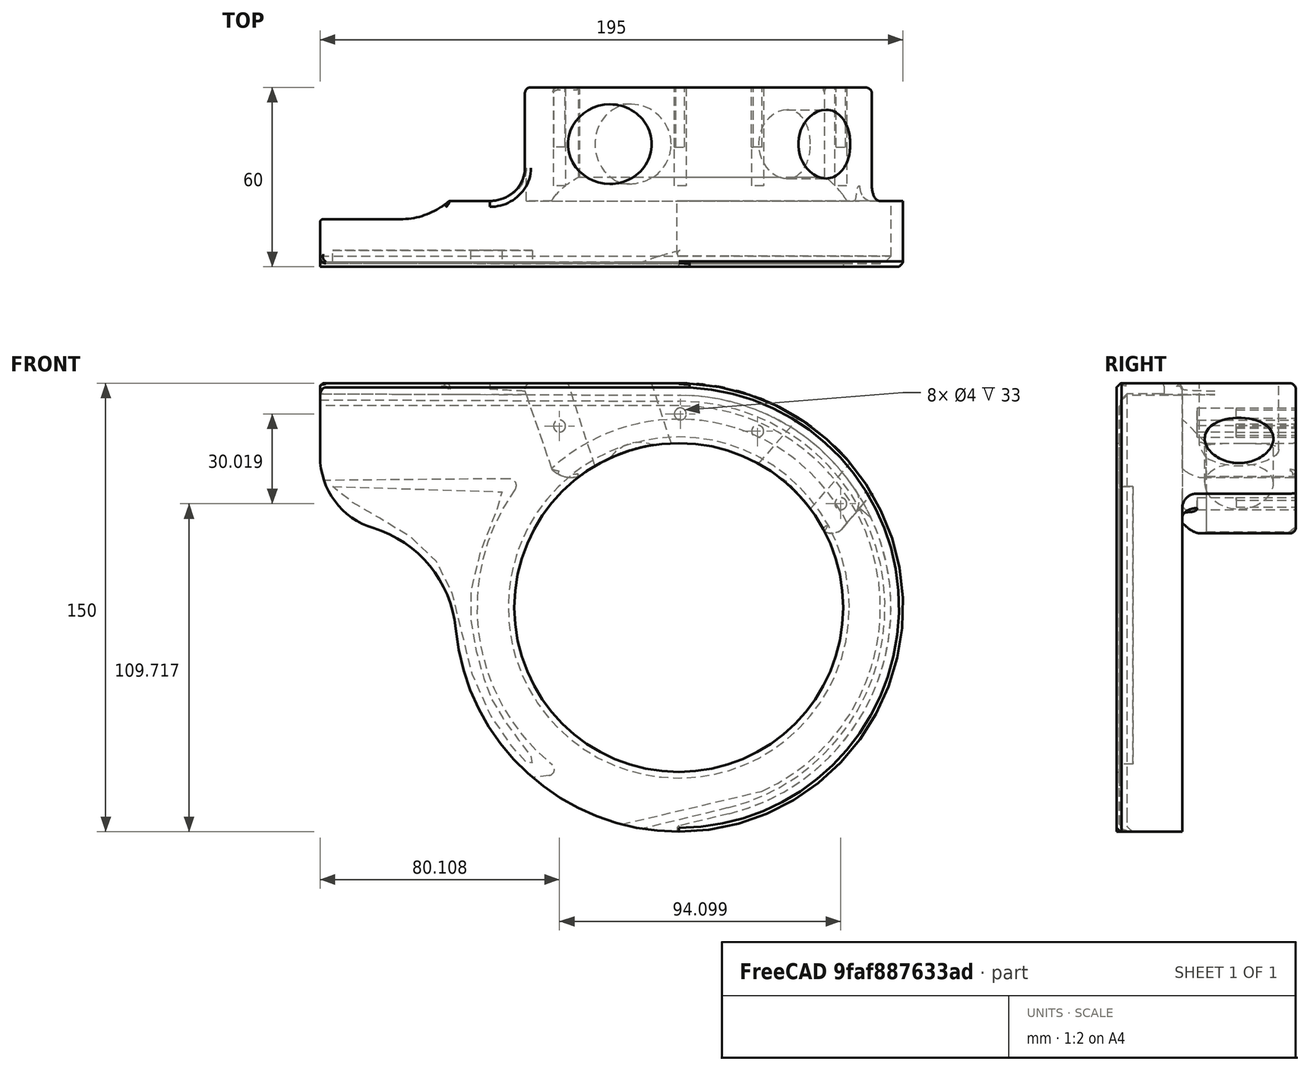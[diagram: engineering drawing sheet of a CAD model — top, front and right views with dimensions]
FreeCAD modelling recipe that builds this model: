
FCSTD DOCUMENT  (FreeCAD 0.19R)
Label: BottomWhiteBike6
License: All rights reserved
LicenseURL: http://en.wikipedia.org/wiki/All_rights_reserved
objects: Sketcher::SketchObject×10, PartDesign::Fillet×9, PartDesign::Pocket×7, PartDesign::Pad×2, Part::Cylinder×2, PartDesign::Chamfer×2, Part::MultiFuse×1, PartDesign::Groove×1, PartDesign::Body×1, Part::Cut×1, Mesh::Feature×1
note: 57 computed .brp shape members not serialized (recipe doc carries the construction recipe); baked Part::Feature solids carry a one-line shape summary decoded from their .brp

FEATURE [Sketcher::SketchObject] Sketch
  FullyConstrained = false
  MapMode = 5
  Placement = pos=(0,0,0) rot=(1,0,0;1.5708rad)
  Support = -> [XZ_Plane]
  sketch-geometry (11):
    g0: LineSegment StartX=0 StartY=0 StartZ=0 EndX=112.706 EndY=65.0706 EndZ=0
    g1: LineSegment StartX=0 StartY=0 StartZ=0 EndX=7.3e-15 EndY=119.149 EndZ=0
    g2: LineSegment StartX=2.14e-14 StartY=70 StartZ=0 EndX=-199.884 EndY=70 EndZ=0
    g3: Circle CenterX=0 CenterY=0 CenterZ=0 NormalX=0 NormalY=0 NormalZ=1 AngleXU=0 Radius=45
    g4: ArcOfCircle CenterX=0 CenterY=0 CenterZ=0 NormalX=0 NormalY=0 NormalZ=1 AngleXU=0 Radius=70 StartAngle=3.5224 EndAngle=7.85398
    g5: LineSegment StartX=-120 StartY=75 StartZ=0 EndX=2.84e-14 EndY=75 EndZ=0
    g6: ArcOfCircle CenterX=0 CenterY=0 CenterZ=0 NormalX=0 NormalY=0 NormalZ=1 AngleXU=0 Radius=75 StartAngle=3.23571 EndAngle=7.85398
    g7: LineSegment StartX=-120 StartY=75 StartZ=0 EndX=-120 EndY=50.5061 EndZ=0
    g8: ArcOfCircle CenterX=-95 CenterY=50.5061 CenterZ=0 NormalX=0 NormalY=0 NormalZ=1 AngleXU=0 Radius=25 StartAngle=3.14159 EndAngle=4.4201
    g9: Circle CenterX=0 CenterY=0 CenterZ=0 NormalX=0 NormalY=0 NormalZ=1 AngleXU=0 Radius=55
    g10: ArcOfCircle CenterX=-113.419 CenterY=-10.7061 CenterZ=0 NormalX=0 NormalY=0 NormalZ=1 AngleXU=0 Radius=38.9235 StartAngle=0.0941155 EndAngle=1.27851
  constraints (25):
    c: Coincident(g0,g-1)
    c: Coincident(g1,g-1)
    c: Angle(g1) = 1.5708
    c: Angle(g0,g1) = 1.0472
    c: PointOnObject(g2,g1)
    c: Angle(g2) = 3.14159
    c: DistanceY(g2) = 70
    c: Coincident(g3,g-1)
    c: Coincident(g4,g-1)
    c: Diameter(g3) = 90
    c: Coincident(g4,g2)
    c: PointOnObject(g5,g1)
    c: Horizontal(g5)
    c: Coincident(g6,g-1)
    c: Coincident(g6,g5)
    c: Coincident(g5,g7)
    c: Vertical(g7)
    c: Tangent(g8,g7) = -1.5708
    c: Diameter(g6) = 150
    c: Distance(g5) = 120
    c: Diameter(g8) = 50
    c: Coincident(g9,g6)
    c: Diameter(g9) = 110
    c: Tangent(g10,g6) = 1.5708
    c: Tangent(g10,g8) = 1.5708
FEATURE [PartDesign::Pad] Pad
  Direction = (1,1,1)
  Length = 40
  Length2 = 20
  Placement = pos=(0,0,0) rot=(1,0,0;1.5708rad)
  Profile = -> Sketch
  Type = 4
FEATURE [Sketcher::SketchObject] Sketch001
  FullyConstrained = false
  MapMode = 5
  Placement = pos=(0,20,-4.4e-15) rot=(-1,0,0;1.5708rad)
  Support = -> [Pad]
  sketch-geometry (14):
    g0: GeomPoint X=0 Y=0 Z=0
    g1: LineSegment StartX=0 StartY=0 StartZ=0 EndX=101.779 EndY=-121.295 EndZ=0
    g2: LineSegment StartX=54.9288 StartY=-26.5684 StartZ=0 EndX=75.9423 EndY=-51.6114 EndZ=0
    g3: ArcOfCircle CenterX=0 CenterY=0 CenterZ=0 NormalX=0 NormalY=0 NormalZ=1 AngleXU=0 Radius=91.8204 StartAngle=5.68627 EndAngle=9.42478
    g4: LineSegment StartX=-211.759 StartY=-107.924 StartZ=0 EndX=-91.8204 EndY=2.84e-14 EndZ=0
    g5: LineSegment StartX=43.6212 StartY=-30.5051 StartZ=0 EndX=-31.6726 EndY=-44.3314 EndZ=0
    g6: LineSegment StartX=-42.2439 StartY=-45.8964 StartZ=0 EndX=-52.4011 EndY=-75.3951 EndZ=0
    g7: LineSegment StartX=0 StartY=0 StartZ=0 EndX=-69.9978 EndY=-203.289 EndZ=0
    g8: ArcOfCircle CenterX=51.1344 CenterY=-29.7522 CenterZ=0 NormalX=0 NormalY=0 NormalZ=1 AngleXU=0 Radius=4.95311 StartAngle=0.698132 EndAngle=2.38613
    g9: LineSegment StartX=47.5288 StartY=-26.3563 StartZ=0 EndX=43.6212 EndY=-30.5051 EndZ=0
    g10: LineSegment StartX=-52.4011 StartY=-75.3951 StartZ=0 EndX=-16.4761 EndY=-75.3951 EndZ=0
    g11: LineSegment StartX=-16.4761 StartY=-75.3951 StartZ=0 EndX=-30.9733 EndY=-107.924 EndZ=0
    g12: LineSegment StartX=-30.9733 StartY=-107.924 StartZ=0 EndX=-211.759 EndY=-107.924 EndZ=0
    g13: ArcOfCircle CenterX=-35.7204 CenterY=-53.4756 CenterZ=0 NormalX=0 NormalY=0 NormalZ=1 AngleXU=0 Radius=10 StartAngle=1.15406 EndAngle=2.28148
  constraints (24):
    c: Coincident(g1,g-1)
    c: Angle(g1,g-2) = 2.44346
    c: Coincident(g3,g-1)
    c: PointOnObject(g3,g-1)
    c: Coincident(g4,g3)
    c: Distance(g2,g1) = 25
    c: Parallel(g2,g1)
    c: Coincident(g7,g3)
    c: Angle(g7,g1) = 1.02974
    c: Parallel(g7,g6)
    c: Distance(g6,g7) = 25
    c: Tangent(g8,g2) = 1.5708
    c: Tangent(g9,g8) = -1.5708
    c: Coincident(g5,g9)
    c: Horizontal(g10)
    c: Coincident(g11,g10)
    c: Coincident(g12,g11)
    c: Coincident(g12,g4)
    c: Horizontal(g12)
    c: Coincident(g6,g13)
    c: Radius(g13) = 10
    c: Coincident(g13,g5)
    c: Coincident(g2,g3)
    c: Coincident(g10,g6)
FEATURE [PartDesign::Pocket] Pocket  label="FirstPocket-trim"
  BaseFeature = -> Pad
  Length = 38
  Length2 = 100
  Placement = pos=(0,0,0) rot=(1,0,0;1.5708rad)
  Profile = -> Sketch001
  Type = 0
FEATURE [Sketcher::SketchObject] Sketch003
  FullyConstrained = false
  MapMode = 5
  Placement = pos=(0,-18,7.9e-15) rot=(-1,0,0;1.5708rad)
  Support = -> [Pocket]
  sketch-geometry (5):
    g0: ArcOfCircle CenterX=0 CenterY=0 CenterZ=0 NormalX=0 NormalY=0 NormalZ=1 AngleXU=0 Radius=71 StartAngle=4.71239 EndAngle=7.61456
    g1: LineSegment StartX=-204.417 StartY=-71.8091 StartZ=0 EndX=0 EndY=-71 EndZ=0
    g2: LineSegment StartX=16.837 StartY=68.9748 StartZ=0 EndX=-53.1835 EndY=86.067 EndZ=0
    g3: LineSegment StartX=-53.1835 StartY=86.067 StartZ=0 EndX=-158.302 EndY=56.4495 EndZ=0
    g4: LineSegment StartX=-158.302 StartY=56.4495 StartZ=0 EndX=-204.417 EndY=-71.8091 EndZ=0
  constraints (8):
    c: Coincident(g0,g-1)
    c: PointOnObject(g0,g-2)
    c: Diameter(g0) = 142
    c: Coincident(g1,g0)
    c: Tangent(g0,g2) = -1.5708
    c: Coincident(g2,g3)
    c: Coincident(g3,g4)
    c: Coincident(g4,g1)
FEATURE [PartDesign::Pocket] Pocket001  label="2ndPocket-thk"
  BaseFeature = -> Pocket
  Length = 20.5
  Length2 = 0
  Placement = pos=(0,0,0) rot=(1,0,0;1.5708rad)
  Profile = -> Sketch003
  Type = 4
FEATURE [Part::Cylinder] Cylinder  label="DT"
  Angle = 360
  AttacherType = Attacher::AttachEngine3D
  Height = 156
  Placement = pos=(1,1,1) rot=(0,1,0;0.715585rad)
  Radius = 11.5
FEATURE [Part::Cylinder] Cylinder001  label="ST"
  Angle = 360
  AttacherType = Attacher::AttachEngine3D
  Height = 150
  Placement = pos=(1,1,1) rot=(0,-1,0;0.314159rad)
  Radius = 13.3
FEATURE [Part::MultiFuse] Fusion
  Shapes = -> [Cylinder,Cylinder001]
FEATURE [Sketcher::SketchObject] Sketch004
  FullyConstrained = false
  MapMode = 5
  Placement = pos=(0,-38,4.2e-14) rot=(0,0.707107,0.707107;3.14159rad)
  sketch-geometry (11):
    g0: ArcOfCircle CenterX=0 CenterY=0 CenterZ=0 NormalX=0 NormalY=0 NormalZ=1 AngleXU=0 Radius=67.4561 StartAngle=1.5708 EndAngle=4.28769
    g1: LineSegment StartX=43.378 StartY=-56.1672 StartZ=0 EndX=97.643 EndY=-63.0707 EndZ=0
    g2: LineSegment StartX=97.643 StartY=-63.0707 StartZ=0 EndX=64.3329 EndY=-83.232 EndZ=0
    g3: LineSegment StartX=64.3329 StartY=-83.232 StartZ=0 EndX=-27.7948 EndY=-61.4636 EndZ=0
    g4: Circle CenterX=0 CenterY=0 CenterZ=0 NormalX=0 NormalY=0 NormalZ=1 AngleXU=0 Radius=57.041
    g5: LineSegment StartX=4.1e-15 StartY=67.4561 StartZ=0 EndX=181.167 EndY=67.4561 EndZ=0
    g6: ArcOfCircle CenterX=0 CenterY=0 CenterZ=0 NormalX=0 NormalY=0 NormalZ=1 AngleXU=0 Radius=67.5078 StartAngle=5.39067 EndAngle=6.9075
    g7: LineSegment StartX=56.6391 StartY=43.0635 StartZ=0 EndX=192.151 EndY=41.8244 EndZ=0
    g8: LineSegment StartX=192.151 StartY=41.8244 StartZ=0 EndX=181.167 EndY=67.4561 EndZ=0
    g9: ArcOfCircle CenterX=56.6183 CenterY=40.7899 CenterZ=0 NormalX=0 NormalY=0 NormalZ=1 AngleXU=0 Radius=2.27364 StartAngle=1.56165 EndAngle=3.7659
    g10: ArcOfCircle CenterX=43.6348 CenterY=-54.1491 CenterZ=0 NormalX=0 NormalY=0 NormalZ=1 AngleXU=0 Radius=2.03437 StartAngle=2.24908 EndAngle=4.58585
  constraints (15):
    c: Coincident(g0,g-1)
    c: Coincident(g2,g1)
    c: Coincident(g3,g2)
    c: Coincident(g3,g0)
    c: Coincident(g4,g0)
    c: PointOnObject(g0,g-2)
    c: Coincident(g5,g0)
    c: Horizontal(g5)
    c: Coincident(g6,g0)
    c: Coincident(g7,g8)
    c: Coincident(g8,g5)
    c: Tangent(g6,g9) = 1.5708
    c: Tangent(g7,g9) = 1.5708
    c: Tangent(g1,g10) = -1.5708
    c: Tangent(g6,g10) = 1.5708
FEATURE [PartDesign::Pocket] Pocket002  label="ChainGroove"
  BaseFeature = -> Pocket001
  Length = 1
  Length2 = 100
  Placement = pos=(0,0,0) rot=(1,0,0;1.5708rad)
  Profile = -> Sketch004
  Type = 0
FEATURE [Sketcher::SketchObject] Sketch006
  FullyConstrained = false
  MapMode = 5
  Placement = pos=(0,20,-1.8e-14) rot=(-1,0,0;1.5708rad)
  sketch-geometry (4):
    g0: Circle CenterX=-39.8919 CenterY=-60.6956 CenterZ=0 NormalX=0 NormalY=0 NormalZ=1 AngleXU=0 Radius=2
    g1: Circle CenterX=0.518637 CenterY=-64.7366 CenterZ=0 NormalX=0 NormalY=0 NormalZ=1 AngleXU=0 Radius=2
    g2: Circle CenterX=26.4007 CenterY=-58.9637 CenterZ=0 NormalX=0 NormalY=0 NormalZ=1 AngleXU=0 Radius=2
    g3: Circle CenterX=54.207 CenterY=-34.7174 CenterZ=0 NormalX=0 NormalY=0 NormalZ=1 AngleXU=0 Radius=2
  constraints (4):
    c: Diameter(g0) = 4
    c: Equal(g0,g1)
    c: Equal(g0,g2)
    c: Equal(g0,g3)
FEATURE [Sketcher::SketchObject] Sketch007
  FullyConstrained = false
  MapMode = 5
  Placement = pos=(0,20,-1.99e-14) rot=(-1,0,0;1.5708rad)
  sketch-geometry (4):
    g0: Circle CenterX=-39.9046 CenterY=-60.6617 CenterZ=0 NormalX=0 NormalY=0 NormalZ=1 AngleXU=0 Radius=2
    g1: Circle CenterX=0.50043 CenterY=-64.7556 CenterZ=0 NormalX=0 NormalY=0 NormalZ=1 AngleXU=0 Radius=2
    g2: Circle CenterX=26.3703 CenterY=-58.9325 CenterZ=0 NormalX=0 NormalY=0 NormalZ=1 AngleXU=0 Radius=2
    g3: Circle CenterX=54.2248 CenterY=-34.7424 CenterZ=0 NormalX=0 NormalY=0 NormalZ=1 AngleXU=0 Radius=2
  constraints (4):
    c: Diameter(g0) = 4
    c: Equal(g0,g1)
    c: Equal(g0,g2)
    c: Equal(g0,g3)
FEATURE [PartDesign::Chamfer] Chamfer
  Angle = 45
  Base = -> Pocket002 [Edge39]
  BaseFeature = -> Pocket002
  ChamferType = 0
  FlipDirection = false
  Placement = pos=(0,0,0) rot=(1,0,0;1.5708rad)
  Size = 2
  Size2 = 1
  SupportTransform = false
FEATURE [PartDesign::Fillet] Fillet
  Base = -> Chamfer [Edge87]
  BaseFeature = -> Chamfer
  Placement = pos=(0,0,0) rot=(1,0,0;1.5708rad)
  Radius = 11
  SupportTransform = false
FEATURE [PartDesign::Chamfer] Chamfer001
  Angle = 45
  Base = -> Fillet [Edge69]
  BaseFeature = -> Fillet
  ChamferType = 0
  FlipDirection = false
  Placement = pos=(0,0,0) rot=(1,0,0;1.5708rad)
  Size = 8
  Size2 = 1
  SupportTransform = false
FEATURE [PartDesign::Fillet] Fillet001
  Base = -> Chamfer001 [Edge35]
  BaseFeature = -> Chamfer001
  Placement = pos=(0,0,0) rot=(1,0,0;1.5708rad)
  Radius = 5
  SupportTransform = false
FEATURE [PartDesign::Fillet] Fillet002
  Base = -> Fillet001 [Edge37]
  BaseFeature = -> Fillet001
  Placement = pos=(0,0,0) rot=(1,0,0;1.5708rad)
  Radius = 1
  SupportTransform = false
FEATURE [PartDesign::Fillet] Fillet003
  Base = -> Fillet002 [Edge31,Edge7,Edge46,Edge32]
  BaseFeature = -> Fillet002
  Placement = pos=(0,0,0) rot=(1,0,0;1.5708rad)
  Radius = 2
  SupportTransform = false
FEATURE [Sketcher::SketchObject] Sketch010
  FullyConstrained = false
  MapMode = 5
  Placement = pos=(-120,0,0) rot=(0.707107,0,-0.707107;3.14159rad)
  Support = -> [Fillet003]
  sketch-geometry (3):
    g0: LineSegment StartX=-75.6145 StartY=37.995 StartZ=0 EndX=-73.0073 EndY=40.6023 EndZ=0
    g1: LineSegment StartX=-73.0073 StartY=40.6023 StartZ=0 EndX=-81.082 EndY=45.6871 EndZ=0
    g2: LineSegment StartX=-81.082 StartY=45.6871 StartZ=0 EndX=-75.6145 EndY=37.995 EndZ=0
  constraints (4):
    c: Coincident(g0,g1)
    c: Coincident(g1,g2)
    c: Coincident(g0,g2)
    c: Angle(g0) = 0.785398
FEATURE [Sketcher::SketchObject] Sketch011
  FullyConstrained = false
  MapMode = 5
  Placement = pos=(0,0,0) rot=(0.57735,0.57735,0.57735;2.0944rad)
  Support = -> [YZ_Plane]
  sketch-geometry (3):
    g0: LineSegment StartX=-36.3196 StartY=77.3765 StartZ=0 EndX=-63.9469 EndY=104.18 EndZ=0
    g1: LineSegment StartX=-63.9469 StartY=104.18 StartZ=0 EndX=-42.5651 EndY=71.1309 EndZ=0
    g2: LineSegment StartX=-42.5651 StartY=71.1309 StartZ=0 EndX=-36.3196 EndY=77.3765 EndZ=0
  constraints (4):
    c: Coincident(g0,g1)
    c: Coincident(g2,g1)
    c: Coincident(g2,g0)
    c: Angle(g2) = 0.785398
FEATURE [PartDesign::Pocket] Pocket003
  BaseFeature = -> Fillet003
  Length = 5
  Length2 = 100
  Placement = pos=(0,0,0) rot=(1,0,0;1.5708rad)
  Profile = -> Sketch010
  Type = 1
FEATURE [PartDesign::Groove] Groove
  Angle = 180
  Axis = (3e-16,1,-2e-16)
  Base = (0,0,0)
  BaseFeature = -> Pocket003
  Placement = pos=(0,0,0) rot=(1,0,0;1.5708rad)
  Profile = -> Sketch011
  ReferenceAxis = -> Sketch011 [H_Axis]
FEATURE [PartDesign::Pocket] Pocket004
  BaseFeature = -> Groove
  Length = 33
  Length2 = 100
  Placement = pos=(0,0,0) rot=(1,0,0;1.5708rad)
  Profile = -> Sketch006
  Type = 0
FEATURE [PartDesign::Pocket] Pocket005
  BaseFeature = -> Pocket004
  Length = 20
  Length2 = 100
  Placement = pos=(0,0,0) rot=(1,0,0;1.5708rad)
  Profile = -> Sketch007
  Type = 0
FEATURE [Sketcher::SketchObject] Sketch012
  FullyConstrained = false
  MapMode = 5
  Placement = pos=(0,-38.5,1.73e-14) rot=(-1,0,0;1.5708rad)
  Support = -> [Pocket005]
  sketch-geometry (47):
    g0-g23: Circle x24 (B-spline internal-alignment scaffolding for g24; pole/knot coordinates omitted)
    g24: BSplineCurve PolesCount=24 KnotsCount=22 Degree=3 IsPeriodic=0
    g25-g46: GeomPoint x22 (B-spline internal-alignment scaffolding for g24; pole/knot coordinates omitted)
  constraints (5):
    c: Weight(g0) = 1
    c: Equal(g0, g1-g23) x23
    c: Coincident(g23,g0)
    c: InternalAlignment(g0-g23 -> g24) x24
    c: InternalAlignment(g25-g46 -> g24) x22
FEATURE [PartDesign::Pad] Pad001
  BaseFeature = -> Pocket005
  Direction = (1,1,1)
  Length = 4
  Length2 = 100
  Placement = pos=(0,0,0) rot=(1,0,0;1.5708rad)
  Profile = -> Sketch012
  Type = 0
FEATURE [PartDesign::Fillet] Fillet004
  Base = -> Pad001 [Edge87]
  BaseFeature = -> Pad001
  Placement = pos=(0,0,0) rot=(1,0,0;1.5708rad)
  Radius = 1
  SupportTransform = false
FEATURE [PartDesign::Fillet] Fillet005
  Base = -> Fillet004 [Edge24]
  BaseFeature = -> Fillet004
  Placement = pos=(0,0,0) rot=(1,0,0;1.5708rad)
  Radius = 1
  SupportTransform = false
FEATURE [PartDesign::Fillet] Fillet006
  Base = -> Fillet005 [Edge137]
  BaseFeature = -> Fillet005
  Placement = pos=(0,0,0) rot=(1,0,0;1.5708rad)
  Radius = 2
  SupportTransform = false
FEATURE [PartDesign::Fillet] Fillet007
  Base = -> Fillet006 [Edge37]
  BaseFeature = -> Fillet006
  Placement = pos=(0,0,0) rot=(1,0,0;1.5708rad)
  Radius = 1
  SupportTransform = false
FEATURE [Sketcher::SketchObject] Sketch013
  FullyConstrained = false
  MapMode = 5
  Placement = pos=(0,3.3e-14,75) rot=(0,0,1;3.14159rad)
  Support = -> [Fillet007]
  sketch-geometry (4):
    g0: LineSegment StartX=165.105 StartY=24.1174 StartZ=0 EndX=93.1616 EndY=24.1174 EndZ=0
    g1: ArcOfCircle CenterX=93.1616 CenterY=-0.882579 CenterZ=0 NormalX=0 NormalY=0 NormalZ=1 AngleXU=0 Radius=25 StartAngle=1.5708 EndAngle=2.82091
    g2: LineSegment StartX=69.4362 StartY=6.99786 StartZ=0 EndX=162.974 EndY=18.3067 EndZ=0
    g3: LineSegment StartX=162.974 StartY=18.3067 StartZ=0 EndX=165.105 EndY=24.1174 EndZ=0
  constraints (6):
    c: Tangent(g1,g0) = -1.5708
    c: Radius(g1) = 25
    c: Coincident(g2,g1)
    c: Horizontal(g0)
    c: Coincident(g3,g2)
    c: Coincident(g3,g0)
FEATURE [PartDesign::Pocket] Pocket006
  BaseFeature = -> Fillet007
  Length = 5
  Length2 = 100
  Placement = pos=(0,0,0) rot=(1,0,0;1.5708rad)
  Profile = -> Sketch013
  Type = 0
FEATURE [PartDesign::Fillet] Fillet008
  Base = -> Pocket006 [Edge23]
  BaseFeature = -> Pocket006
  Placement = pos=(0,0,0) rot=(1,0,0;1.5708rad)
  Radius = 1
  SupportTransform = false
FEATURE [PartDesign::Body] Body
  Group = -> [Sketch,Pad,Sketch001,Pocket,Sketch003,Pocket001,Sketch004,Pocket002,Sketch006,Sketch007,Chamfer,Fillet,Chamfer001,Fillet001,Fillet002,Fillet003,Sketch010,Sketch011,Pocket003,Groove,Pocket004,Pocket005,Sketch012,Pad001,Fillet004,Fillet005,Fillet006,Fillet007,Sketch013,Pocket006,Fillet008]
  Origin = -> Origin
  Tip = -> Fillet008
FEATURE [Part::Cut] Cut
  Base = -> Fillet008
  Tool = -> Fusion
FEATURE [Mesh::Feature] Mesh  label="Cut (Meshed)"
